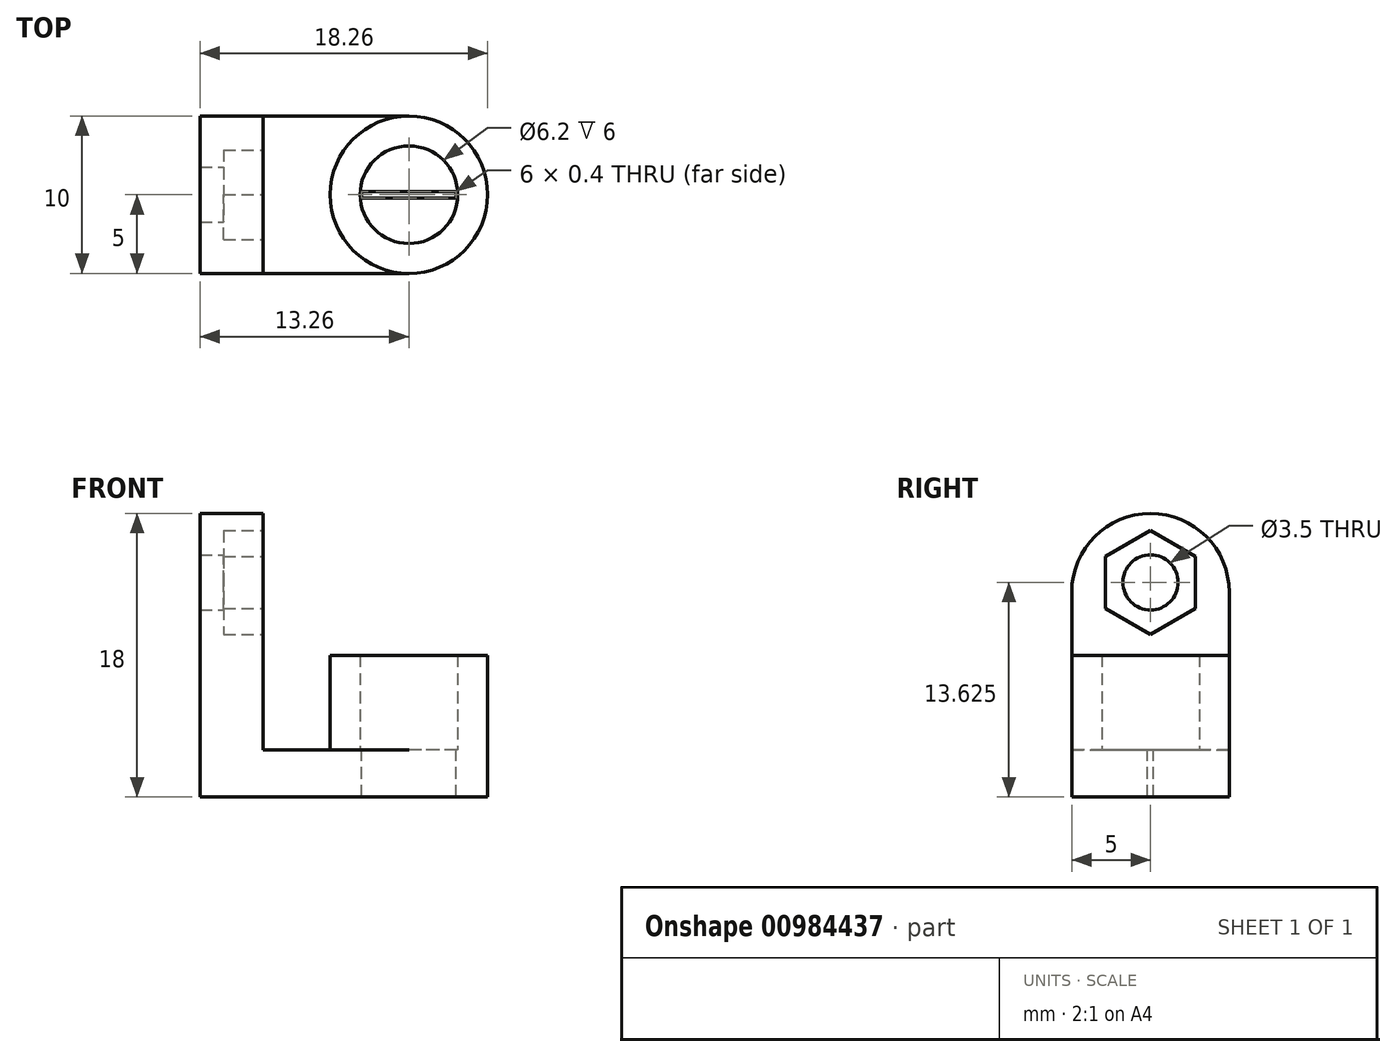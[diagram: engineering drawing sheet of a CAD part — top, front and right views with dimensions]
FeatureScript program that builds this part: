
annotation { "Feature Type Name" : "Feature", "Feature Type Description" : "" }
export const myFeature = defineFeature(function(context is Context, id is Id, definition is map)
    precondition{}
    {
        {
            var Q0;
            Q0=qCreatedBy(makeId("Top.planeOp"),FACE);
            var sketch = newSketch(context, id + "F0", { "sketchPlane" : qUnion([Q0])});
            skCircle(sketch, "E0", {"center": v(0, 0) * mm, "radius": 5 * mm});
            skCircle(sketch, "E1", {"center": v(0, 0) * mm, "radius": 3.1 * mm});
            skCircle(sketch, "E2", {"center": v(0, 0) * mm, "radius": 1 * mm});
            skLineSegment(sketch, "E3.bottom", {"start": v(0, -5) * mm, "end": v(-13.26, -5) * mm});
            skLineSegment(sketch, "E3.top", {"start": v(0, 5) * mm, "end": v(-13.26, 5) * mm});
            skLineSegment(sketch, "E3.right", {"start": v(-13.26, -5) * mm, "end": v(-13.26, 5) * mm});
            skSolve(sketch);
        }
        {
            var Q0;
            Q0=makeQuery(id+"F0.imprint","IMPRINT",FACE,{"disambiguationData":[TD([[makeQuery(id+"F0.imprint","IMPRINT",EDGE,{"derivedFrom":sQuery(id+"F0.wireOp",EDGE,"E0")}),1.0]])]});
            var Q1;
            Q1=makeQuery(id+"F0.imprint","IMPRINT",FACE,{"disambiguationData":[TD([[makeQuery(id+"F0.imprint","IMPRINT",EDGE,{"derivedFrom":sQuery(id+"F0.wireOp",EDGE,"E1")}),1.0]])]});
            var Q2;
            {var subQ0=sQuery(id+"F0.wireOp",EDGE,"E3.bottom");Q2=makeQuery(id+"F0.imprint","IMPRINT",FACE,{"disambiguationData":[TD([[makeQuery(id+"F0.imprint","IMPRINT",EDGE,{"derivedFrom":subQ0}),-1.0]])]});}
            var Q3;
            Q3=makeQuery(id+"F0.imprint","IMPRINT",FACE,{"disambiguationData":[TD([[makeQuery(id+"F0.imprint","IMPRINT",EDGE,{"derivedFrom":sQuery(id+"F0.wireOp",EDGE,"E2")}),1.0]])]});
            extrude(context, id + "F1", {"entities" : qUnion([Q0, Q1, Q2, Q3]), "oppositeDirection" : true, "depth" : 3 * mm, "offsetDistance" : 25 * mm});
        }
        {
            var Q0;
            Q0=makeQuery(id+"F0.imprint","IMPRINT",FACE,{"disambiguationData":[TD([[makeQuery(id+"F0.imprint","IMPRINT",EDGE,{"derivedFrom":sQuery(id+"F0.wireOp",EDGE,"E0")}),1.0]])]});
            extrude(context, id + "F2", {"entities" : qUnion([Q0]), "operationType" : NewBodyOperationType.ADD, "depth" : 6 * mm, "offsetDistance" : 25 * mm});
        }
        {
            var Q0;
            {var subQ0=sQuery(id+"F0.wireOp",EDGE,"E3.right");var subQ1=sQuery(id+"F0.wireOp",EDGE,"E3.bottom");var subQ2=sQuery(id+"F0.wireOp",EDGE,"E0");var subQ3=sQuery(id+"F0.wireOp",EDGE,"E3.top");Q0=makeQuery(id+"F2.boolean.opBoolean","SPLIT",FACE,{"disambiguationData":[TD([makeQuery(id+"F1.opExtrude","SWEPT_FACE",FACE,{"disambiguationData":[OSD([subQ2])]})])],"derivedFrom":makeQuery(id+"F1.opExtrude","CAP_FACE",FACE,{"disambiguationData":[OSD([subQ2,sQuery(id+"F0.wireOp",EDGE,"E2"),subQ1,subQ3,subQ0])],"isStart":true})});}
            var sketch = newSketch(context, id + "F3", { "sketchPlane" : qUnion([Q0])});
            skLineSegment(sketch, "E4.bottom", {"start": v(-13.26, -5) * mm, "end": v(-9.26, -5) * mm});
            skLineSegment(sketch, "E4.top", {"start": v(-13.26, 5) * mm, "end": v(-9.26, 5) * mm});
            skLineSegment(sketch, "E4.left", {"start": v(-13.26, -5) * mm, "end": v(-13.26, 5) * mm});
            skLineSegment(sketch, "E4.right", {"start": v(-9.26, -5) * mm, "end": v(-9.26, 5) * mm});
            skSolve(sketch);
        }
        {
            var Q0;
            Q0 = qSketchRegion(id + "F3", true);
            extrude(context, id + "F4", {"entities" : qUnion([Q0]), "operationType" : NewBodyOperationType.ADD, "depth" : 15 * mm, "offsetDistance" : 25 * mm});
        }
        {
            var Q0;
            Q0=makeQuery(id+"F4.opExtrude","SWEPT_FACE",FACE,{"disambiguationData":[OSD([sQuery(id+"F3.wireOp",EDGE,"E4.right")])]});
            var sketch = newSketch(context, id + "F5", { "sketchPlane" : qUnion([Q0])});
            skCircle(sketch, "E5", {"center": v(0, 10.63) * mm, "radius": 1.75 * mm});
            skPoint(sketch, "E5.centerSnap0", {"position": v(0, 15) * mm});
            skSolve(sketch);
        }
        {
            var Q0;
            Q0 = qSketchRegion(id + "F5", true);
            extrude(context, id + "F6", {"entities" : qUnion([Q0]), "operationType" : NewBodyOperationType.REMOVE, "oppositeDirection" : true, "depth" : 25 * mm, "offsetDistance" : 25 * mm});
        }
        {
            var Q0;
            Q0=makeQuery(id+"F4.opExtrude","SWEPT_FACE",FACE,{"disambiguationData":[OSD([sQuery(id+"F3.wireOp",EDGE,"E4.right")])]});
            var sketch = newSketch(context, id + "F7", { "sketchPlane" : qUnion([Q0])});
            skCircle(sketch, "E6.cCircle", {"center": v(0, 10.63) * mm, "radius": 2.85 * mm, "construction": true});
            skLineSegment(sketch, "E6.0", {"start": v(2.85, 8.98) * mm, "end": v(0, 7.33) * mm});
            skLineSegment(sketch, "E6.1", {"start": v(0, 7.33) * mm, "end": v(-2.85, 8.98) * mm});
            skLineSegment(sketch, "E6.2", {"start": v(-2.85, 8.98) * mm, "end": v(-2.85, 12.27) * mm});
            skLineSegment(sketch, "E6.3", {"start": v(-2.85, 12.27) * mm, "end": v(0, 13.92) * mm});
            skLineSegment(sketch, "E6.4", {"start": v(0, 13.92) * mm, "end": v(2.85, 12.27) * mm});
            skLineSegment(sketch, "E6.5", {"start": v(2.85, 12.27) * mm, "end": v(2.85, 8.98) * mm});
            skPoint(sketch, "E6.0.midPoint", {"position": v(1.43, 8.16) * mm});
            skSolve(sketch);
        }
        {
            var Q0;
            Q0 = qSketchRegion(id + "F7", true);
            extrude(context, id + "F8", {"entities" : qUnion([Q0]), "operationType" : NewBodyOperationType.REMOVE, "oppositeDirection" : true, "depth" : 2.5 * mm, "offsetDistance" : 25 * mm});
        }
        {
            var Q0;
            Q0=makeQuery(id+"F4.opExtrude","CAP_EDGE",EDGE,{"disambiguationData":[OSD([sQuery(id+"F3.wireOp",EDGE,"E4.bottom")])],"isStart":false});
            var Q1;
            Q1=makeQuery(id+"F4.opExtrude","CAP_EDGE",EDGE,{"disambiguationData":[OSD([sQuery(id+"F3.wireOp",EDGE,"E4.top")])],"isStart":false});
            fillet(context, id + "F9", {"entities" : qUnion([Q0, Q1]), "radius" : 5 * mm, "tangentPropagation" : true, "allowEdgeOverflow" : false});
        }
        {
            var Q0;
            Q0=makeQuery(id+"F2.boolean.opBoolean","SPLIT",FACE,{"disambiguationData":[TD([makeQuery(id+"F2.opExtrude","SWEPT_FACE",FACE,{"disambiguationData":[OSD([sQuery(id+"F0.wireOp",EDGE,"E1")])]})])],"derivedFrom":makeQuery(id+"F1.opExtrude","CAP_FACE",FACE,{"disambiguationData":[OSD([sQuery(id+"F0.wireOp",EDGE,"E0"),sQuery(id+"F0.wireOp",EDGE,"E3.bottom"),sQuery(id+"F0.wireOp",EDGE,"E3.top"),sQuery(id+"F0.wireOp",EDGE,"E3.right")])],"isStart":true})});
            var sketch = newSketch(context, id + "F10", { "sketchPlane" : qUnion([Q0])});
            skLineSegment(sketch, "E7.bottom", {"start": v(3, 0.2) * mm, "end": v(-3, 0.2) * mm});
            skLineSegment(sketch, "E7.top", {"start": v(3, -0.2) * mm, "end": v(-3, -0.2) * mm});
            skLineSegment(sketch, "E7.left", {"start": v(3, 0.2) * mm, "end": v(3, -0.2) * mm});
            skLineSegment(sketch, "E7.right", {"start": v(-3, 0.2) * mm, "end": v(-3, -0.2) * mm});
            skPoint(sketch, "E7.middle", {"position": v(0, 0) * mm});
            skSolve(sketch);
        }
        {
            var Q0;
            Q0 = qSketchRegion(id + "F10", true);
            extrude(context, id + "F11", {"entities" : qUnion([Q0]), "operationType" : NewBodyOperationType.REMOVE, "oppositeDirection" : true, "depth" : 25 * mm, "offsetDistance" : 25 * mm});
        }
    });
